# Revit family: Skylight-Wasco-Single_Pitch
name_source: partatom
category: Windows
revit_build: Autodesk Revit Architecture 2013 (Build: 20130531_2115(x64)
units: mm (PartAtom-declared; Revit-internal decimal feet)

## types (3) — shared parameters
Curb = Rubber - Wasco - Black
Description = Skylight
Finish = Aluminum - Wasco - Aged Copper
Glazing 1 5_16 = No
Glazing Material = Glass - Wasco - Clear
Manufacturer = Wasco
Number of Purlins = 2
Product Documentation Link = http://www.wascoskylights.com
Product Name = Single Pitch
Product Page URL = http://www.wascoskylights.com
URL = http://www.wascoskylights.com

## per-type parameters (varying)
| type | Curb Height | Curb Width | Default Elevation | Glazing Area | Glazing Thickness | Height | Host Length | Host Width | Hypotenuse | Length | Pinnacle | Purlin | Rafter Array | Rafter Depth | Rough Height | Rough Width | Sill Height Offset | Sill Width Offset | Single Pitch Height | Single Pitch Width | Width | Width Actual |
| Pinnacle 350 | 0' - 5" | 0' - 4" | 9' - 8 1/4" | 22.63 SF | 0' - 1 1/16" | 9' - 9 1/32" | 20' - 0" | 11' - 0" | 10' - 5 5/8" | 18' - 0" | Base Plate - Sill : 350 | No | 3 | 0' - 5" | 10' - 2 1/32" | 9' - 4 3/8" | 0' - 0 17/32" | 0' - 5 31/32" | 9' - 4 3/8" | 9' - 4 3/8" | 9' - 0" | 9' - 0" |
| Pinnacle 600 | 0' - 3 1/32" | 0' - 4" | 19' - 8 5/16" | 69.01 SF | 0' - 1 3/16" | 11' - 11 7/32" | 40' - 0" | 21' - 0" | 14' - 10 9/16" | 38' - 0" | Base Plate - Sill : 600 | No | 4 | 0' - 7 7/8" | 12' - 2 1/4" | 19' - 4 13/32" | 0' - 0 17/32" | 0' - 5 31/32" | 11' - 3 9/16" | 19' - 4 13/32" | 19' - 0" | 19' - 0" |
| Pinnacle 900 | 0' - 6" | 0' - 6" | 23' - 3 3/32" | 140.62 SF | 0' - 1 3/16" | 23' - 5 11/16" | 16' - 0" | 10' - 0" | 25' - 5 13/16" | 14' - 0" | Base Plate - Sill : 900 | Yes | 4 | 0' - 10 3/4" | 23' - 11 11/16" | 22' - 9 17/32" | 0' - 0 5/8" | 0' - 5 3/4" | 22' - 9 17/32" | 22' - 9 17/32" | 8' - 0" | 8' - 0" |

note: column(s) folded — value = type name in every type: Model

type visibility flags: 3 boolean params named "<type name>" — each type sets only its own to Yes (folded from table)

## geometry (parser evidence)
native form markers: Blend x12, Sweep x22
no freeform markers — native parametric forms only
